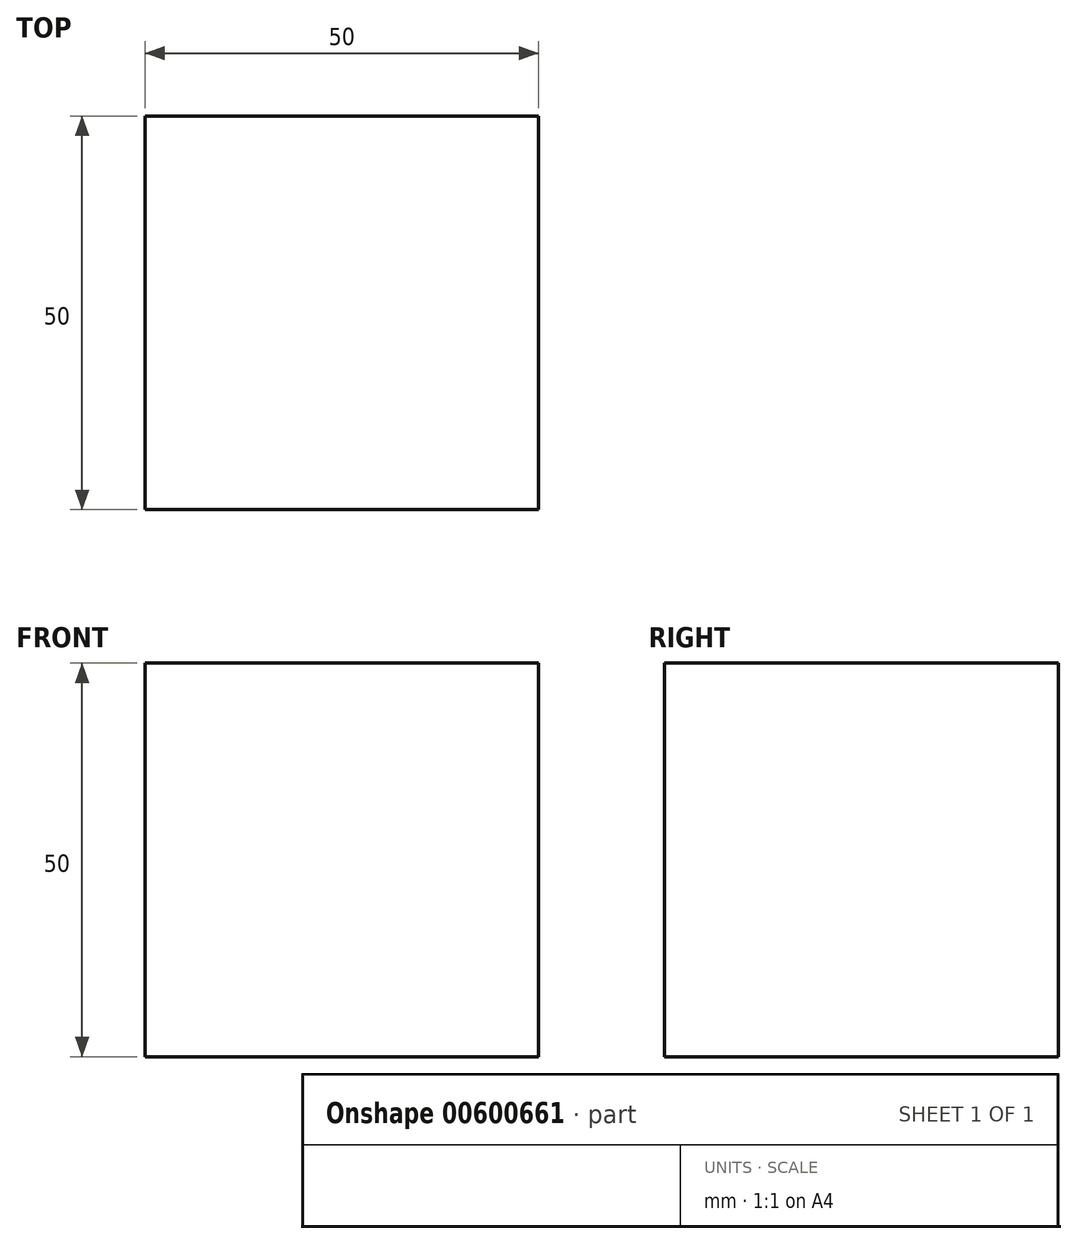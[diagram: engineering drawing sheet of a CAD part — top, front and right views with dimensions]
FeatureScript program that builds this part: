
annotation { "Feature Type Name" : "Feature", "Feature Type Description" : "" }
export const myFeature = defineFeature(function(context is Context, id is Id, definition is map)
    precondition{}
    {
        {
            var Q0;
            Q0=qCreatedBy(makeId("Top.planeOp"),FACE);
            var sketch = newSketch(context, id + "F0", { "sketchPlane" : qUnion([Q0])});
            skLineSegment(sketch, "E0.bottom", {"start": v(-25, 25) * mm, "end": v(25, 25) * mm});
            skLineSegment(sketch, "E0.top", {"start": v(-25, -25) * mm, "end": v(25, -25) * mm});
            skLineSegment(sketch, "E0.left", {"start": v(-25, 25) * mm, "end": v(-25, -25) * mm});
            skLineSegment(sketch, "E0.right", {"start": v(25, 25) * mm, "end": v(25, -25) * mm});
            skPoint(sketch, "E0.middle", {"position": v(0, 0) * mm});
            skSolve(sketch);
        }
        {
            var Q0;
            Q0 = qSketchRegion(id + "F0", true);
            extrude(context, id + "F1", {"entities" : qUnion([Q0]), "endBound" : BoundingType.SYMMETRIC, "depth" : 50 * mm, "offsetDistance" : 25 * mm});
        }
    });
